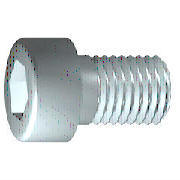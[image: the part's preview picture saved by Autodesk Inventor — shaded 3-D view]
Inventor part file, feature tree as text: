
AUTODESK INVENTOR PART (.ipt)
format: ipt  version: 2015 (Build 190159000, 159)  size: 198,144 bytes
history: native  units: mm (DEFAULTED — no unit token found)
features: sketch x2, extrude x1, plane x1, fillet x1
ambient origin geometry x7: Origin, YZ Plane, XY Plane, X Axis, Y Axis, Z Axis, Center Point
bodies: Solid1 (feature_tree), Body (feature_tree)
feature tree (5):
  extrude  "Slot"  Depth=5.0mm
  plane  "Work Plane1"
  fillet  "Fillet2"  Radius=5.0mm
  sketch  "Sketch1"  dims[d1=14.0mm d2=0.49086mm d3=5.0mm]
  sketch  "Sketch2"  dims[d4=2.5mm d5=60.0deg d6=5.0mm d7=5.0mm d8=4.618802mm d9=8.5mm d10=90.0deg d11=10.0mm d12=0.0mm d13=14.0mm d14=0.0mm d15=0.49076mm d16=0.49076mm d17=0.5mm d19=0.0mm d26=16.0mm d27=45.0deg d28=0.0mm d29=0.0mm d30=0.1mm]
